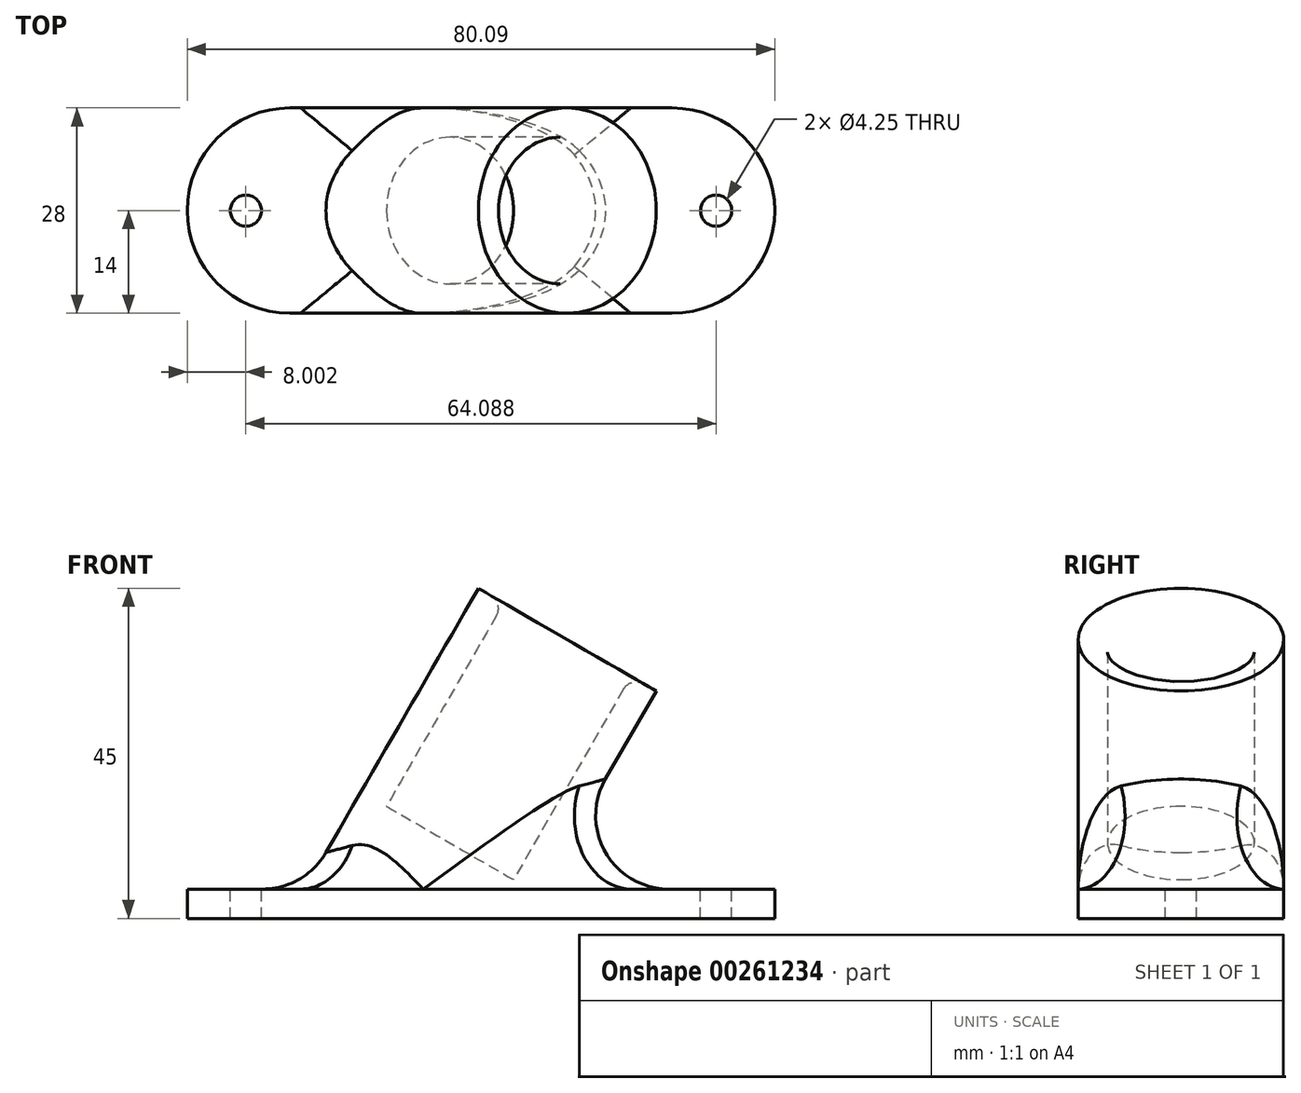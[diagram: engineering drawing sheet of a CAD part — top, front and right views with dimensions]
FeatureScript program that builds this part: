
annotation { "Feature Type Name" : "Feature", "Feature Type Description" : "" }
export const myFeature = defineFeature(function(context is Context, id is Id, definition is map)
    precondition{}
    {
        {
            var Q0;
            Q0=qCreatedBy(makeId("Front.planeOp"),FACE);
            var sketch = newSketch(context, id + "F0", { "sketchPlane" : qUnion([Q0])});
            skPoint(sketch, "E0", {"position": v(-30, 0) * mm});
            skPoint(sketch, "E1", {"position": v(30, 0) * mm});
            skLineSegment(sketch, "E2", {"start": v(-30, 0) * mm, "end": v(30, 0) * mm, "construction": true});
            skLineSegment(sketch, "E3", {"start": v(0, 0) * mm, "end": v(30.9, 44.14) * mm, "construction": true});
            skLineSegment(sketch, "E4", {"start": v(0, 0) * mm, "end": v(0, 38) * mm, "construction": true});
            skLineSegment(sketch, "E5", {"start": v(0, 38) * mm, "end": v(26.6, 38) * mm, "construction": true});
            skPoint(sketch, "E6", {"position": v(26.6, 38) * mm});
            skLineSegment(sketch, "E7", {"start": v(0, 0) * mm, "end": v(35.36, 61.25) * mm, "construction": true});
            skSolve(sketch);
        }
        {
            var Q0;
            Q0=qCreatedBy(makeId("Front.planeOp"),FACE);
            var sketch = newSketch(context, id + "F1", { "sketchPlane" : qUnion([Q0])});
            skLineSegment(sketch, "E8", {"start": v(0, 0) * mm, "end": v(0, 5) * mm});
            skLineSegment(sketch, "E9.0", {"start": v(0, 0) * mm, "end": v(35.36, 61.25) * mm});
            skPoint(sketch, "E10", {"position": v(21.94, 38) * mm});
            skLineSegment(sketch, "E11", {"start": v(13.28, 43) * mm, "end": v(9.82, 45) * mm});
            skLineSegment(sketch, "E12", {"start": v(9.82, 45) * mm, "end": v(-17.93, -3.05) * mm});
            skLineSegment(sketch, "E13", {"start": v(-17.93, -3.05) * mm, "end": v(-14.47, -5.05) * mm});
            skLineSegment(sketch, "E14", {"start": v(-14.47, -5.05) * mm, "end": v(13.28, 43) * mm});
            skSolve(sketch);
        }
        {
            var Q0;
            Q0=makeQuery(id+"F1.imprint","IMPRINT",FACE,{"disambiguationData":[TD([[makeQuery(id+"F1.imprint","IMPRINT",EDGE,{"derivedFrom":sQuery(id+"F1.wireOp",EDGE,"E11")}),1.0]])]});
            var Q1;
            Q1=sQuery(id+"F1.wireOp",EDGE,"E9.0");
            revolve(context, id + "F2", {"entities" : qUnion([Q0]), "axis" : qUnion([Q1]), "revolveType" : RevolveType.FULL});
        }
        {
            var Q0;
            Q0=qCreatedBy(makeId("Top.planeOp"),FACE);
            cPlane(context, id + "F3", {"entities" : qUnion([Q0]), "cplaneType" : CPlaneType.OFFSET, "offset" : 4 * mm, "width" : 150 * mm, "height" : 150 * mm});
        }
        {
            var Q0;
            Q0=qCreatedBy(id+"F3.planeOp",FACE);
            var sketch = newSketch(context, id + "F4", { "sketchPlane" : qUnion([Q0])});
            skLineSegment(sketch, "E15", {"start": v(-29.88, 14) * mm, "end": v(-29.88, -14) * mm});
            skLineSegment(sketch, "E16", {"start": v(50.21, 14) * mm, "end": v(50.21, -14) * mm});
            skLineSegment(sketch, "E17", {"start": v(-29.88, 14) * mm, "end": v(50.21, 14) * mm});
            skLineSegment(sketch, "E18", {"start": v(-29.88, -14) * mm, "end": v(50.21, -14) * mm});
            skSolve(sketch);
        }
        {
            var Q0;
            Q0=makeQuery(id+"F4.imprint","IMPRINT",FACE,{"disambiguationData":[TD([[makeQuery(id+"F4.imprint","IMPRINT",EDGE,{"derivedFrom":sQuery(id+"F4.wireOp",EDGE,"E15")}),1.0]])]});
            extrude(context, id + "F5", {"entities" : qUnion([Q0]), "operationType" : NewBodyOperationType.ADD, "oppositeDirection" : true, "depth" : 4 * mm});
        }
        {
            var Q0;
            Q0=makeQuery(id+"F5.opExtrude","SWEPT_EDGE",EDGE,{"disambiguationData":[OSD([sQuery(id+"F4.wireOp",EDGE,"E16"),sQuery(id+"F4.wireOp",EDGE,"E18")])]});
            var Q1;
            Q1=makeQuery(id+"F5.opExtrude","SWEPT_EDGE",EDGE,{"disambiguationData":[OSD([sQuery(id+"F4.wireOp",EDGE,"E16"),sQuery(id+"F4.wireOp",EDGE,"E17")])]});
            var Q2;
            Q2=makeQuery(id+"F5.opExtrude","SWEPT_EDGE",EDGE,{"disambiguationData":[OSD([sQuery(id+"F4.wireOp",EDGE,"E15"),sQuery(id+"F4.wireOp",EDGE,"E18")])]});
            var Q3;
            Q3=makeQuery(id+"F5.opExtrude","SWEPT_EDGE",EDGE,{"disambiguationData":[OSD([sQuery(id+"F4.wireOp",EDGE,"E15"),sQuery(id+"F4.wireOp",EDGE,"E17")])]});
            fillet(context, id + "F6", {"entities" : qUnion([Q0, Q1, Q2, Q3]), "radius" : 14 * mm, "tangentPropagation" : true, "allowEdgeOverflow" : false});
        }
        {
            var Q0;
            {var subQ0=sQuery(id+"F4.wireOp",EDGE,"E18");var subQ1=sQuery(id+"F4.wireOp",EDGE,"E17");var subQ2=sQuery(id+"F4.wireOp",EDGE,"E15");var subQ3=makeQuery(id+"F5.opExtrude","CAP_FACE",FACE,{"disambiguationData":[OSD([subQ2,sQuery(id+"F4.wireOp",EDGE,"E16"),subQ1,subQ0])],"isStart":true});Q0=makeQuery(id+"F5.boolean.opBoolean","SPLIT",FACE,{"disambiguationData":[TD([makeQuery(id+"F5.opExtrude","SWEPT_FACE",FACE,{"disambiguationData":[OSD([subQ2])]})])],"derivedFrom":subQ3});}
            var sketch = newSketch(context, id + "F7", { "sketchPlane" : qUnion([Q0])});
            skPoint(sketch, "E19.endSnap0", {"position": v(-29.88, 0) * mm});
            skCircle(sketch, "E20", {"center": v(-21.88, 0) * mm, "radius": 2.12 * mm});
            skSolve(sketch);
        }
        {
            var Q0;
            Q0=makeQuery(id+"F7.imprint","IMPRINT",FACE,{"disambiguationData":[TD([[makeQuery(id+"F7.imprint","IMPRINT",EDGE,{"derivedFrom":sQuery(id+"F7.wireOp",EDGE,"E20")}),1.0]])]});
            var Q1;
            Q1=sQuery(id+"F7.wireOp",EDGE,"E20");
            extrude(context, id + "F8", {"entities" : qUnion([Q0]), "operationType" : NewBodyOperationType.REMOVE, "surfaceEntities" : qUnion([Q1]), "oppositeDirection" : true, "depth" : 5 * mm});
        }
        {
            var Q0;
            {var subQ0=sQuery(id+"F4.wireOp",EDGE,"E17");var subQ1=sQuery(id+"F4.wireOp",EDGE,"E18");var subQ2=sQuery(id+"F4.wireOp",EDGE,"E16");var subQ3=makeQuery(id+"F5.opExtrude","CAP_FACE",FACE,{"disambiguationData":[OSD([sQuery(id+"F4.wireOp",EDGE,"E15"),subQ2,subQ0,subQ1])],"isStart":true});Q0=makeQuery(id+"F5.boolean.opBoolean","SPLIT",FACE,{"disambiguationData":[TD([makeQuery(id+"F5.opExtrude","SWEPT_FACE",FACE,{"disambiguationData":[OSD([subQ2])]})])],"derivedFrom":subQ3});}
            var sketch = newSketch(context, id + "F9", { "sketchPlane" : qUnion([Q0])});
            skPoint(sketch, "E21.endSnap0", {"position": v(50.21, 0) * mm});
            skCircle(sketch, "E22", {"center": v(42.21, 0) * mm, "radius": 2.12 * mm});
            skSolve(sketch);
        }
        {
            var Q0;
            Q0=makeQuery(id+"F9.imprint","IMPRINT",FACE,{"disambiguationData":[TD([[makeQuery(id+"F9.imprint","IMPRINT",EDGE,{"derivedFrom":sQuery(id+"F9.wireOp",EDGE,"E22")}),1.0]])]});
            extrude(context, id + "F10", {"entities" : qUnion([Q0]), "operationType" : NewBodyOperationType.REMOVE, "oppositeDirection" : true, "depth" : 5 * mm});
        }
        {
            var Q0;
            Q0=makeQuery(id+"F2.opRevolve","SWEPT_FACE",FACE,{"disambiguationData":[OSD([sQuery(id+"F1.wireOp",EDGE,"E11")])]});
            cPlane(context, id + "F11", {"entities" : qUnion([Q0]), "cplaneType" : CPlaneType.OFFSET, "offset" : 32 * mm, "oppositeDirection" : true, "width" : 150 * mm, "height" : 150 * mm});
        }
        {
            var Q0;
            Q0=qCreatedBy(id+"F11.planeOp",FACE);
            var sketch = newSketch(context, id + "F12", { "sketchPlane" : qUnion([Q0])});
            skPoint(sketch, "E23.0", {"position": v(0, 0) * mm});
            skCircle(sketch, "E24", {"center": v(0, 0) * mm, "radius": 10.5 * mm});
            skSolve(sketch);
        }
        {
            var Q0;
            Q0=makeQuery(id+"F12.imprint","IMPRINT",FACE,{"disambiguationData":[TD([[makeQuery(id+"F12.imprint","IMPRINT",EDGE,{"derivedFrom":sQuery(id+"F12.wireOp",EDGE,"E24")}),1.0]])]});
            extrude(context, id + "F13", {"entities" : qUnion([Q0]), "operationType" : NewBodyOperationType.ADD, "oppositeDirection" : true, "depth" : 22 * mm});
        }
        {
            var Q0;
            Q0=qCreatedBy(makeId("Front.planeOp"),FACE);
            var sketch = newSketch(context, id + "F14", { "sketchPlane" : qUnion([Q0])});
            skLineSegment(sketch, "E25.0", {"start": v(-30, 0) * mm, "end": v(30, 0) * mm});
            skLineSegment(sketch, "E26.bottom", {"start": v(-20.63, 0) * mm, "end": v(17.45, 0) * mm});
            skLineSegment(sketch, "E26.top", {"start": v(-20.63, -17.9) * mm, "end": v(17.45, -17.9) * mm});
            skLineSegment(sketch, "E26.left", {"start": v(-20.63, 0) * mm, "end": v(-20.63, -17.9) * mm});
            skLineSegment(sketch, "E26.right", {"start": v(17.45, 0) * mm, "end": v(17.45, -17.9) * mm});
            skSolve(sketch);
        }
        {
            var Q0;
            Q0=makeQuery(id+"F14.imprint","IMPRINT",FACE,{"disambiguationData":[TD([[makeQuery(id+"F14.imprint","IMPRINT",EDGE,{"derivedFrom":sQuery(id+"F14.wireOp",EDGE,"E26.top")}),1.0]])]});
            extrude(context, id + "F15", {"entities" : qUnion([Q0]), "operationType" : NewBodyOperationType.REMOVE, "endBound" : BoundingType.SYMMETRIC, "depth" : 30 * mm});
        }
        {
            var Q0;
            Q0=makeQuery(id+"F5.boolean.opBoolean","INTERSECT",EDGE,{"disambiguationData":[OD(0.0)],"derivedFrom":[makeQuery(id+"F2.opRevolve","SWEPT_FACE",FACE,{"disambiguationData":[OSD([sQuery(id+"F1.wireOp",EDGE,"E12")])]}),makeQuery(id+"F5.opExtrude","CAP_FACE",FACE,{"disambiguationData":[OSD([sQuery(id+"F4.wireOp",EDGE,"E15"),sQuery(id+"F4.wireOp",EDGE,"E16"),sQuery(id+"F4.wireOp",EDGE,"E17"),sQuery(id+"F4.wireOp",EDGE,"E18")])],"isStart":true})]});
            fillet(context, id + "F16", {"entities" : qUnion([Q0]), "radius" : 10 * mm, "tangentPropagation" : true, "allowEdgeOverflow" : false});
        }
        {
            var Q0;
            Q0=makeQuery(id+"F2.opRevolve","SWEPT_EDGE",EDGE,{"disambiguationData":[OSD([sQuery(id+"F1.wireOp",EDGE,"E11"),sQuery(id+"F1.wireOp",EDGE,"E14")])]});
            fillet(context, id + "F17", {"entities" : qUnion([Q0]), "radius" : 2 * mm, "tangentPropagation" : true, "allowEdgeOverflow" : false});
        }
    });
